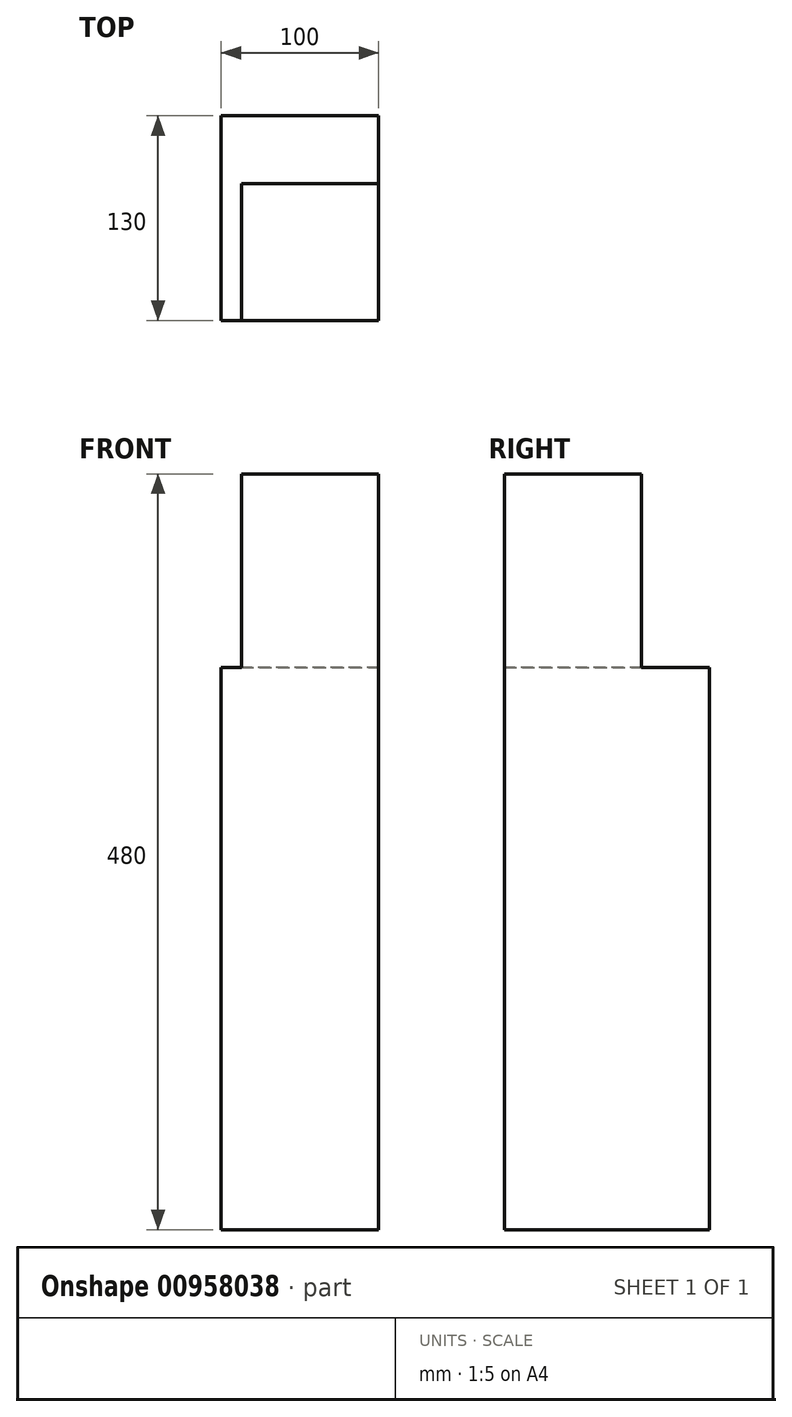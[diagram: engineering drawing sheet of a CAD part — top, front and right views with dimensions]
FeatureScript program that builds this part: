
annotation { "Feature Type Name" : "Feature", "Feature Type Description" : "" }
export const myFeature = defineFeature(function(context is Context, id is Id, definition is map)
    precondition{}
    {
        {
            var Q0;
            Q0=qCreatedBy(makeId("Top.planeOp"),FACE);
            var sketch = newSketch(context, id + "F0", { "sketchPlane" : qUnion([Q0])});
            skLineSegment(sketch, "E0.bottom", {"start": v(50, -65) * mm, "end": v(-50, -65) * mm});
            skLineSegment(sketch, "E0.top", {"start": v(50, 65) * mm, "end": v(-50, 65) * mm});
            skLineSegment(sketch, "E0.left", {"start": v(50, -65) * mm, "end": v(50, 65) * mm});
            skLineSegment(sketch, "E0.right", {"start": v(-50, -65) * mm, "end": v(-50, 65) * mm});
            skPoint(sketch, "E0.middle", {"position": v(0, 0) * mm});
            skSolve(sketch);
        }
        {
            var Q0;
            Q0=makeQuery(id+"F0.imprint","IMPRINT",FACE,{"disambiguationData":[TD([[makeQuery(id+"F0.imprint","IMPRINT",EDGE,{"derivedFrom":sQuery(id+"F0.wireOp",EDGE,"E0.bottom")}),-1.0]])]});
            extrude(context, id + "F1", {"entities" : qUnion([Q0]), "depth" : 480 * mm, "offsetDistance" : 25 * mm});
        }
        {
            var Q0;
            Q0=makeQuery(id+"F1.opExtrude","CAP_FACE",FACE,{"disambiguationData":[OSD([sQuery(id+"F0.wireOp",EDGE,"E0.bottom"),sQuery(id+"F0.wireOp",EDGE,"E0.top"),sQuery(id+"F0.wireOp",EDGE,"E0.left"),sQuery(id+"F0.wireOp",EDGE,"E0.right")])],"isStart":false});
            var sketch = newSketch(context, id + "F2", { "sketchPlane" : qUnion([Q0])});
            skLineSegment(sketch, "E1.bottom", {"start": v(-50, 65) * mm, "end": v(50, 65) * mm});
            skLineSegment(sketch, "E1.top", {"start": v(-50, 22) * mm, "end": v(50, 22) * mm});
            skLineSegment(sketch, "E1.left", {"start": v(-50, 65) * mm, "end": v(-50, 22) * mm});
            skLineSegment(sketch, "E1.right", {"start": v(50, 65) * mm, "end": v(50, 22) * mm});
            skLineSegment(sketch, "E2.bottom", {"start": v(-50, 65) * mm, "end": v(-37, 65) * mm});
            skLineSegment(sketch, "E2.top", {"start": v(-50, -65) * mm, "end": v(-37, -65) * mm});
            skLineSegment(sketch, "E2.left", {"start": v(-50, 65) * mm, "end": v(-50, -65) * mm});
            skLineSegment(sketch, "E2.right", {"start": v(-37, 65) * mm, "end": v(-37, -65) * mm});
            skSolve(sketch);
        }
        {
            var Q0;
            {var subQ0=sQuery(id+"F2.wireOp",EDGE,"E1.bottom");Q0=makeQuery(id+"F2.imprint","IMPRINT",FACE,{"disambiguationData":[TD([[makeQuery(id+"F2.imprint","IMPRINT",EDGE,{"derivedFrom":subQ0}),1.0]])]});}
            var Q1;
            {var subQ5=sQuery(id+"F2.wireOp",EDGE,"E2.bottom");Q1=makeQuery(id+"F2.imprint","IMPRINT",FACE,{"disambiguationData":[TD([[makeQuery(id+"F2.imprint","IMPRINT",EDGE,{"derivedFrom":subQ5}),1.0]])]});}
            var Q2;
            {var subQ5=sQuery(id+"F2.wireOp",EDGE,"E2.top");Q2=makeQuery(id+"F2.imprint","IMPRINT",FACE,{"disambiguationData":[TD([[makeQuery(id+"F2.imprint","IMPRINT",EDGE,{"derivedFrom":subQ5}),-1.0]])]});}
            extrude(context, id + "F3", {"entities" : qUnion([Q0, Q1, Q2]), "operationType" : NewBodyOperationType.REMOVE, "oppositeDirection" : true, "depth" : 123 * mm, "offsetDistance" : 25 * mm});
        }
    });
